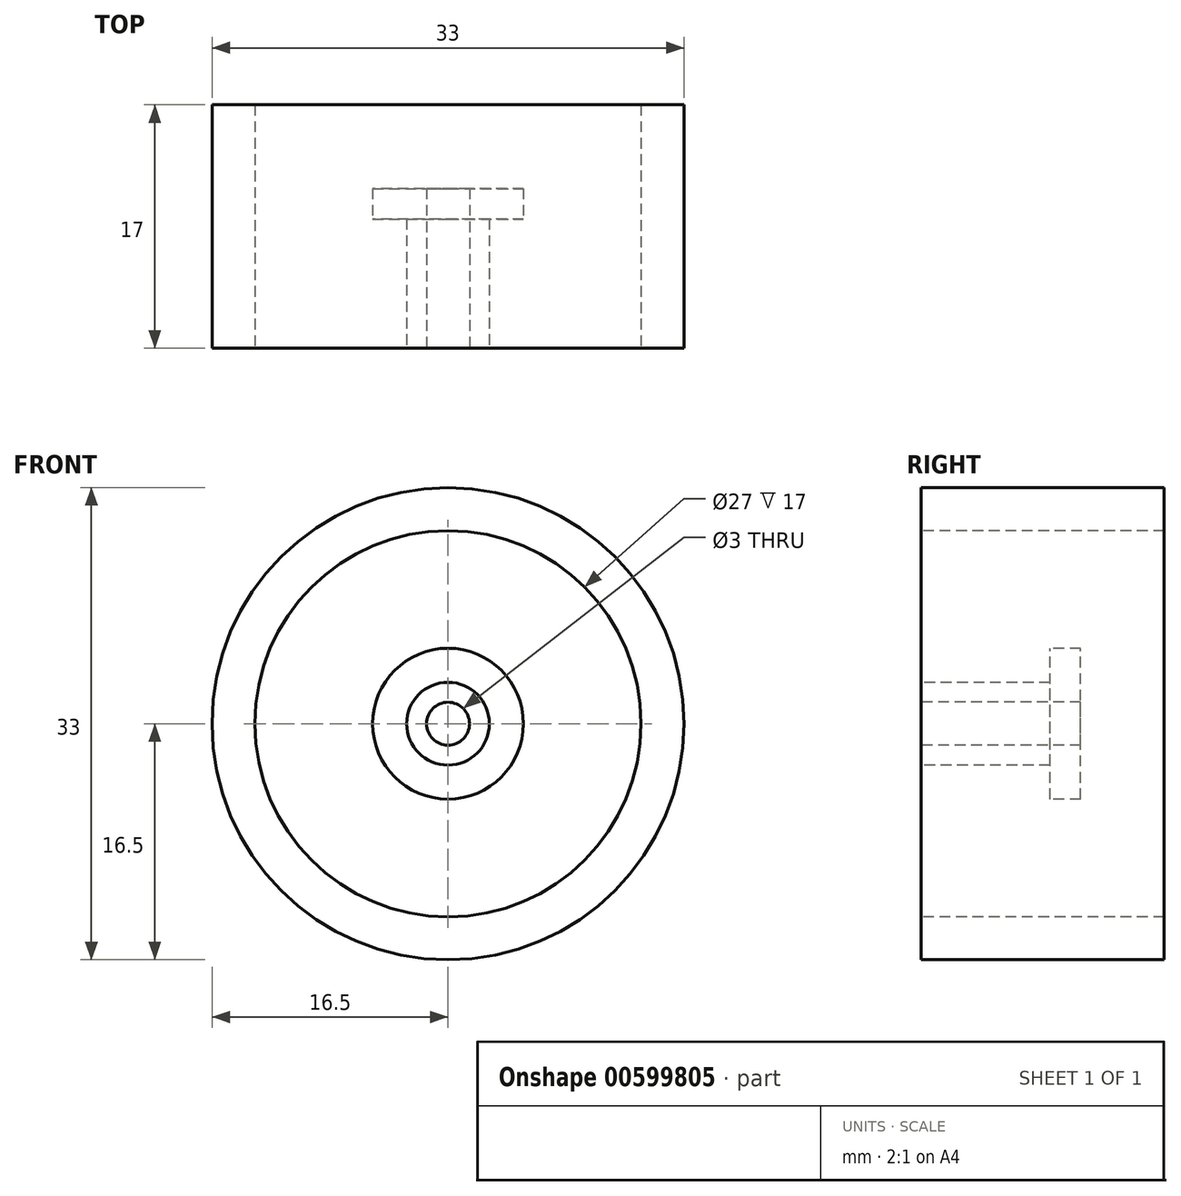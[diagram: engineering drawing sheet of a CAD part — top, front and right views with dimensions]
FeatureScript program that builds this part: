
annotation { "Feature Type Name" : "Feature", "Feature Type Description" : "" }
export const myFeature = defineFeature(function(context is Context, id is Id, definition is map)
    precondition{}
    {
        {
            var Q0;
            Q0=qCreatedBy(makeId("Right.planeOp"),FACE);
            var sketch = newSketch(context, id + "F0", { "sketchPlane" : qUnion([Q0])});
            skLineSegment(sketch, "E0.bottom", {"start": v(0, 0) * mm, "end": v(17, 0) * mm});
            skLineSegment(sketch, "E0.top", {"start": v(0, 16.5) * mm, "end": v(17, 16.5) * mm});
            skLineSegment(sketch, "E0.left", {"start": v(0, 0) * mm, "end": v(0, 16.5) * mm});
            skLineSegment(sketch, "E0.right", {"start": v(17, 0) * mm, "end": v(17, 16.5) * mm});
            skLineSegment(sketch, "E1", {"start": v(17, 13.5) * mm, "end": v(0, 13.5) * mm});
            skLineSegment(sketch, "E2", {"start": v(0, 1.5) * mm, "end": v(11.16, 1.5) * mm});
            skLineSegment(sketch, "E3", {"start": v(11.16, 1.5) * mm, "end": v(11.16, 5.27) * mm});
            skLineSegment(sketch, "E4", {"start": v(11.16, 5.27) * mm, "end": v(9.02, 5.27) * mm});
            skLineSegment(sketch, "E5", {"start": v(9.02, 5.27) * mm, "end": v(9.02, 2.9) * mm});
            skLineSegment(sketch, "E6", {"start": v(9.02, 2.9) * mm, "end": v(0, 2.9) * mm});
            skLineSegment(sketch, "E7", {"start": v(0, 2.9) * mm, "end": v(0, 1.5) * mm});
            skSolve(sketch);
        }
        {
            var Q0;
            {var subQ0=sQuery(id+"F0.wireOp",EDGE,"E0.top");Q0=makeQuery(id+"F0.imprint","IMPRINT",FACE,{"disambiguationData":[TD([[makeQuery(id+"F0.imprint","IMPRINT",EDGE,{"derivedFrom":subQ0}),-1.0]])]});}
            var Q1;
            Q1=makeQuery(id+"F0.imprint","IMPRINT",FACE,{"disambiguationData":[TD([[makeQuery(id+"F0.imprint","IMPRINT",EDGE,{"derivedFrom":sQuery(id+"F0.wireOp",EDGE,"E2")}),1.0]])]});
            var Q2;
            Q2=sQuery(id+"F0.wireOp",EDGE,"E0.bottom");
            revolve(context, id + "F1", {"entities" : qUnion([Q0, Q1]), "axis" : qUnion([Q2]), "revolveType" : RevolveType.FULL});
        }
    });
